# Revit family: Lighting_Pendants_Zero_Silo_Trio_Pendant
name_source: partatom
category: Lighting Fixtures
units: mm (PartAtom-declared; Revit-internal decimal feet)

## family parameters
Always vertical = Yes
Cut with Voids When Loaded = No
Light Source = Yes
OmniClass Number = 23.80.70.00
OmniClass Title = Lighting
Part Type = Normal
Room Calculation Point = No
Round Connector Dimension = Use Diameter
Shared = No
Work Plane-Based = Yes

## types (7) — shared parameters
AssetType = Fixed
BIMObjectName = Lighting_Pendants_Zero_Silo_Trio_Pendant
Brand = Zero
Brand url = http://www.zero.se
Category = Pendant
Collection = Silo Trio
Color Filter = 16777215
Description = This year the minimalistic pendant inspired by a grain silo’s classical silhouette has grown into a family
Design country = Sweden
Designer = Note Design Studio
Dimming Lamp Color Temperature Shift = <None>
DurationUnit = Year
Edition number = 1
Features = Terminal block 2x2,25mm2. Installation: Ceiling-hook. 2 m wire pendant.
Finish = Painted aluminum and steel. Diffusor in matt acrylic.
HasProtectiveEarth = No
IP_Code = IP20
IfcExportAs = IfcLightFixtureType
IfcExportType = NOTDEFINED
LightFixtureMountingType = Suspended
LightFixturePlacingType = Ceiling
Manufacturer = Zero
Manufacturer country = Sweden
Manufacturer name = ZERO
ManufacturerName = Zero
ManufacturerURL = https://www.zerolighting.com
Material = Aluminium and steel
Material main = Aluminium
Material secondary = Steel
NBSDescription = General purpose luminaires
NBSReference = 90-60-50/405
Name = Zero_Silo_Trio_Pendant
Nominal height = 230 mm
Nominal width = 150 mm
NominalCurrent = 0 A
NominalDiameter = 150 mm
NominalFrequencyRange = 50 Hz
NominalLength = 1050 mm  [stored 3.44488 ft]
NominalRadius = 75 mm  [stored 0.246063 ft]
NominalVoltage = 230 V
NominalVoltageCalc = 0 V
NumberOfPoles = 1
PhaseAngle = 0.00°
Photometric Web File = SiloTrio8207-LED_IES.IES
Product Guid = 57f2f5ac-32a3-4da8-8c39-74f8435d3940
Product SKU = Silo_Trio_pendant
Product family = Silo Trio
Product group = Pendant
ProductInformation = This year the minimalistic pendant inspired by a grain silo’s classical silhouette has grown into a family
Revision = 5
Shape = Sculptured
Size = 1050x150x230 mm
Tilt Angle = 90.00°
TotalWattage = 20 W
URL = https://www.zerolighting.com
Uniclass2 = Pr_70_70_49_86
Uniclass2015Description = Suspended luminaires
Uniclass2015Reference = Pr_70_70_48_86
UsageCurrent = 0 A
Version = 3
VersionDate = 31/08/2023
WarrantyDurationUnit = Year
Weight Net (Kg) = 2.5
zero-valued in all types: DefaultElevation, ElectricalDeviceNominalPower, MaintenanceFactor, NumberOfSources

## per-type parameters (varying)
| type | ArticleNumber | Color | LightFixtureMainMaterial | ModelNumber |
| Silo Trio 3 x Max20W/E27 White | 8207-3-17 | Pink | White RAL 9010 | 8207-3-17 |
| Silo Trio 3 x Max20W/E27 Black | 8207-3-06 | Black | Black RAL 9005 | 8207-3-06 |
| Silo Trio 3 x Max20W/E27 Grey | 8207-3-11 | Grey | Grey RAL 7030 | 8207-3-11 |
| Silo Trio 3 x Max20W/E27 Green | 8207-3-12 | Green | Green RAL 6021 | 8207-3-12 |
| Silo Trio 3 x Max20W/E27 Yellow | 8207-3-14 | Yellow | Yellow RAL 1018 | 8207-3-14 |
| Silo Trio 3 x Max20W/E27 Apricot | 8207-3-17 | Pink | Apricot RAL 3012 | 8207-3-17 |
| Silo Trio 3 x Max20W/E27 Ivory | 8207-3-46 | Ivory | Ivory RAL 1015 | 8207-3-46 |

note: column(s) folded — value = type name in every type: Model

note: [stored X ft] marks values corroborated as IEEE doubles in the binary element streams (Revit-internal decimal feet)

## geometry (parser evidence)
native form markers: Sweep x9
no freeform markers — native parametric forms only
